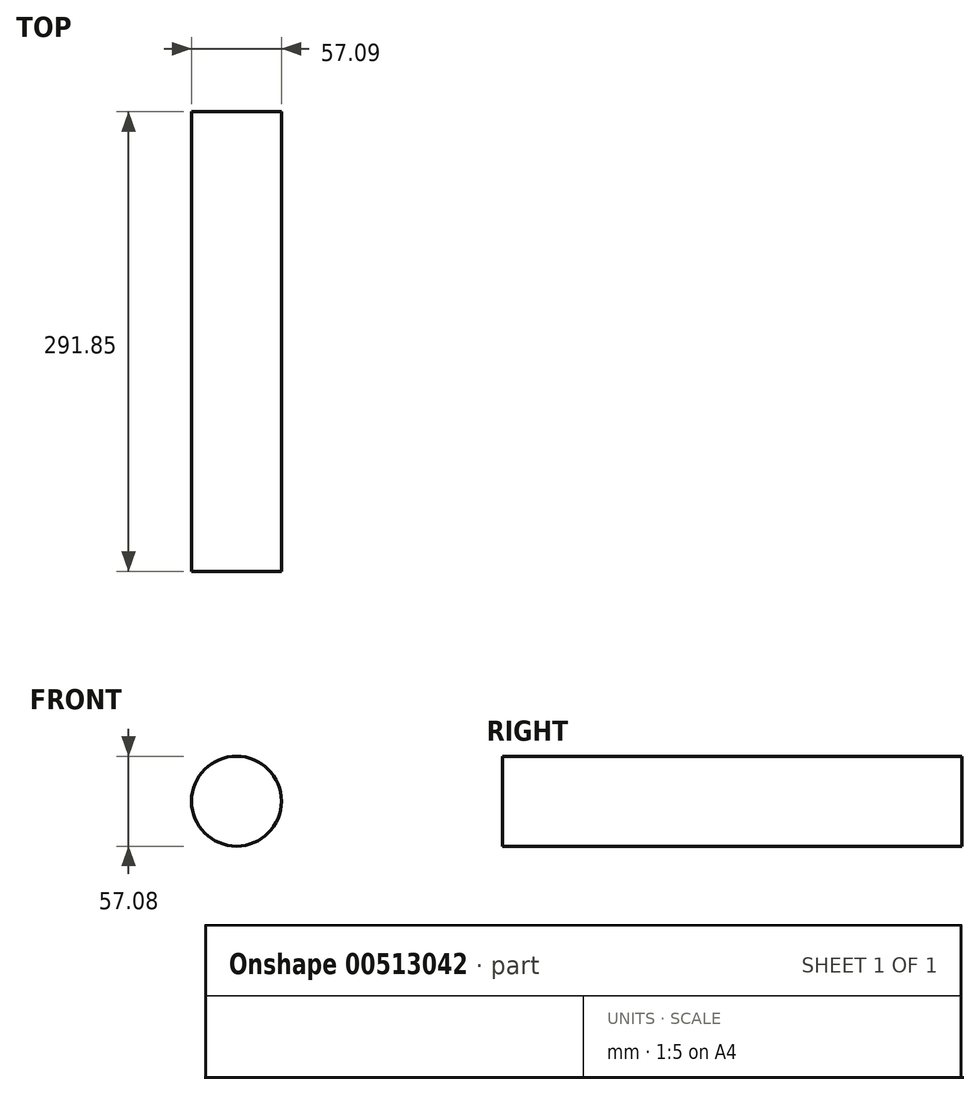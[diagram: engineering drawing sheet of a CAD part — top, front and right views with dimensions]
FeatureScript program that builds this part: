
annotation { "Feature Type Name" : "Feature", "Feature Type Description" : "" }
export const myFeature = defineFeature(function(context is Context, id is Id, definition is map)
    precondition{}
    {
        {
            var Q0;
            Q0=qCreatedBy(makeId("Front.planeOp"),FACE);
            var sketch = newSketch(context, id + "F0", { "sketchPlane" : qUnion([Q0])});
            skCircle(sketch, "E0", {"center": v(-3.87, 0) * mm, "radius": 28.54 * mm});
            skSolve(sketch);
        }
        {
            var Q0;
            Q0=makeQuery(id+"F0.imprint","IMPRINT",FACE,{"disambiguationData":[TD([[makeQuery(id+"F0.imprint","IMPRINT",EDGE,{"derivedFrom":sQuery(id+"F0.wireOp",EDGE,"E0")}),1.0]])]});
            extrude(context, id + "F1", {"entities" : qUnion([Q0]), "depth" : 291.85 * mm});
        }
    });
